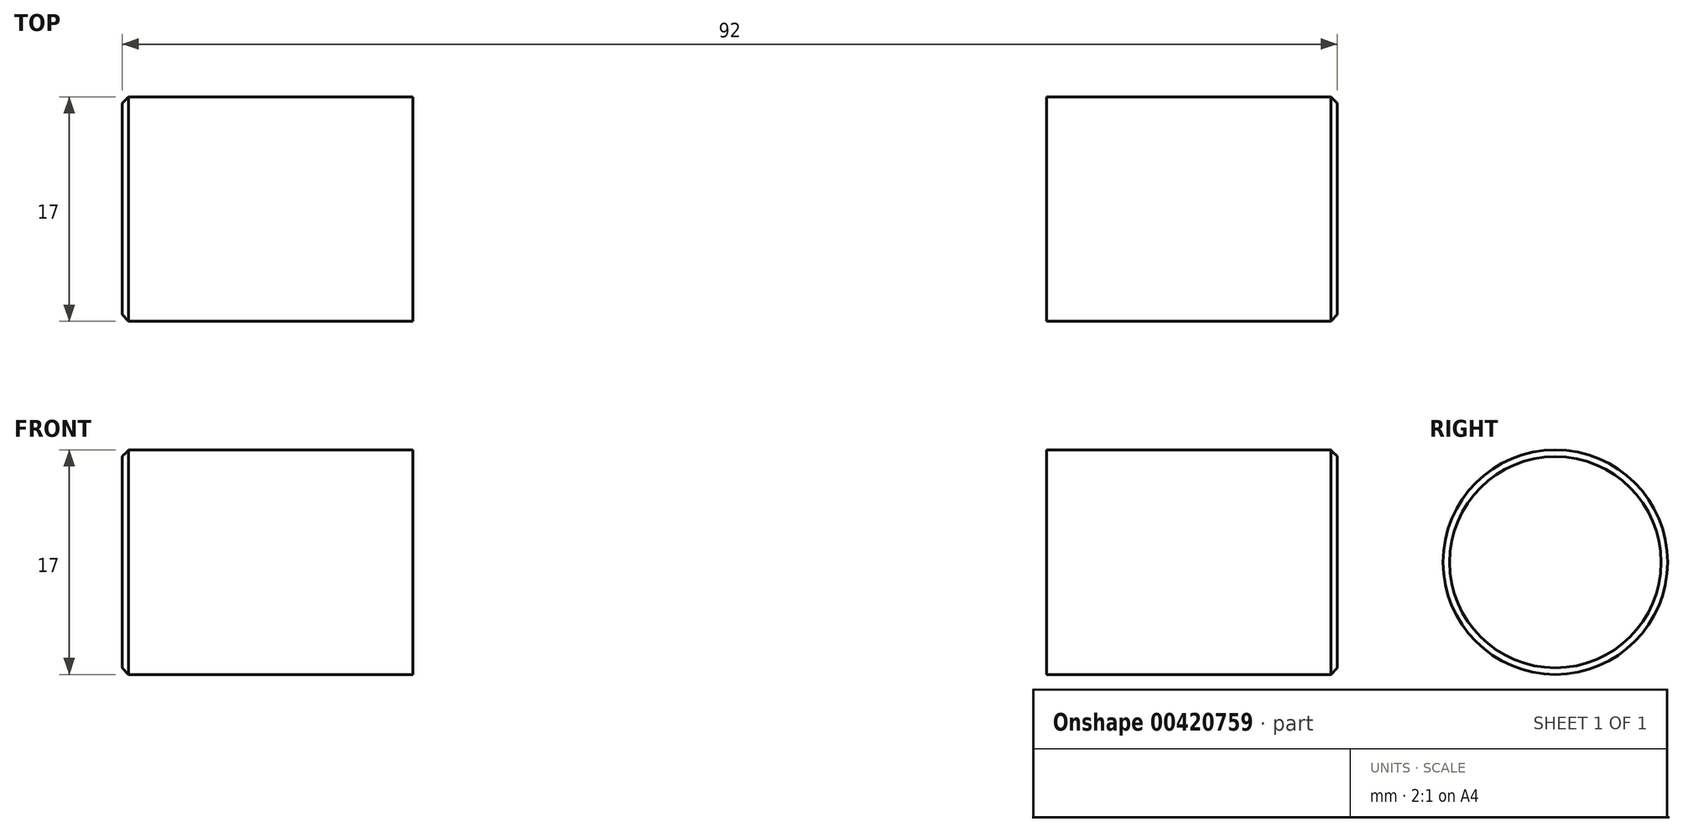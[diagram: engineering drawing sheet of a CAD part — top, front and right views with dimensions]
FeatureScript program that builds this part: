
annotation { "Feature Type Name" : "Feature", "Feature Type Description" : "" }
export const myFeature = defineFeature(function(context is Context, id is Id, definition is map)
    precondition{}
    {
        {
            var Q0;
            Q0=qCreatedBy(makeId("Front.planeOp"),FACE);
            var sketch = newSketch(context, id + "F0", { "sketchPlane" : qUnion([Q0])});
            skLineSegment(sketch, "E0.bottom", {"start": v(-46, 0) * mm, "end": v(46, 0) * mm});
            skLineSegment(sketch, "E0.top", {"start": v(-46, 8.5) * mm, "end": v(-24, 8.5) * mm});
            skLineSegment(sketch, "E0.left", {"start": v(-46, 0) * mm, "end": v(-46, 8.5) * mm});
            skLineSegment(sketch, "E0.right", {"start": v(46, 0) * mm, "end": v(46, 8.5) * mm});
            skLineSegment(sketch, "E1.bottom", {"start": v(-24, 0) * mm, "end": v(24, 0) * mm});
            skLineSegment(sketch, "E1.top", {"start": v(-24, 10) * mm, "end": v(24, 10) * mm});
            skLineSegment(sketch, "E1.left", {"start": v(-24, 0) * mm, "end": v(-24, 10) * mm});
            skLineSegment(sketch, "E1.right", {"start": v(24, 0) * mm, "end": v(24, 10) * mm});
            skLineSegment(sketch, "E2.trimOffspring", {"start": v(24, 8.5) * mm, "end": v(46, 8.5) * mm});
            skSolve(sketch);
        }
        {
            var Q0;
            {var subQ4=sQuery(id+"F0.wireOp",EDGE,"E0.top");Q0=makeQuery(id+"F0.imprint","IMPRINT",FACE,{"disambiguationData":[TD([[makeQuery(id+"F0.imprint","IMPRINT",EDGE,{"derivedFrom":subQ4}),-1.0]])]});}
            var Q1;
            {var subQ3=sQuery(id+"F0.wireOp",EDGE,"E1.bottom");Q1=makeQuery(id+"F0.imprint","IMPRINT",FACE,{"disambiguationData":[TD([[makeQuery(id+"F0.imprint","IMPRINT",EDGE,{"derivedFrom":subQ3}),1.0]])]});}
            var Q2;
            {var subQ0=sQuery(id+"F0.wireOp",EDGE,"E0.right");Q2=makeQuery(id+"F0.imprint","IMPRINT",FACE,{"disambiguationData":[TD([[makeQuery(id+"F0.imprint","IMPRINT",EDGE,{"derivedFrom":subQ0}),1.0]])]});}
            var Q3;
            Q3=sQuery(id+"F0.wireOp",EDGE,"E0.bottom");
            revolve(context, id + "F1", {"entities" : qUnion([Q0, Q1, Q2]), "axis" : qUnion([Q3]), "revolveType" : RevolveType.FULL});
        }
        {
            var Q0;
            Q0=makeQuery(id+"F1.opRevolve","SWEPT_EDGE",EDGE,{"disambiguationData":[OSD([sQuery(id+"F0.wireOp",EDGE,"E0.top"),sQuery(id+"F0.wireOp",EDGE,"E0.left")])]});
            var Q1;
            Q1=makeQuery(id+"F1.opRevolve","SWEPT_EDGE",EDGE,{"disambiguationData":[OSD([sQuery(id+"F0.wireOp",EDGE,"E0.right"),sQuery(id+"F0.wireOp",EDGE,"E2.trimOffspring")])]});
            chamfer(context, id + "F2", {"entities" : qUnion([Q0, Q1]), "width" : 0.5 * mm, "tangentPropagation" : true});
        }
        {
            var Q0;
            Q0=qCreatedBy(makeId("Front.planeOp"),FACE);
            cPlane(context, id + "F3", {"entities" : qUnion([Q0]), "cplaneType" : CPlaneType.OFFSET, "offset" : 7 * mm, "width" : 150 * mm, "height" : 150 * mm});
        }
        {
            var Q0;
            Q0=qCreatedBy(id+"F3.planeOp",FACE);
            var sketch = newSketch(context, id + "F4", { "sketchPlane" : qUnion([Q0])});
            skLineSegment(sketch, "E3.bottom", {"start": v(-15, 2.5) * mm, "end": v(15, 2.5) * mm});
            skLineSegment(sketch, "E3.top", {"start": v(-15, -2.5) * mm, "end": v(15, -2.5) * mm});
            skLineSegment(sketch, "E3.left", {"start": v(-15, 2.5) * mm, "end": v(-15, -2.5) * mm});
            skLineSegment(sketch, "E3.right", {"start": v(15, 2.5) * mm, "end": v(15, -2.5) * mm});
            skSolve(sketch);
        }
        {
            var Q0;
            Q0 = qSketchRegion(id + "F4", true);
            extrude(context, id + "F5", {"entities" : qUnion([Q0]), "operationType" : NewBodyOperationType.REMOVE, "depth" : mm});
        }
    });
